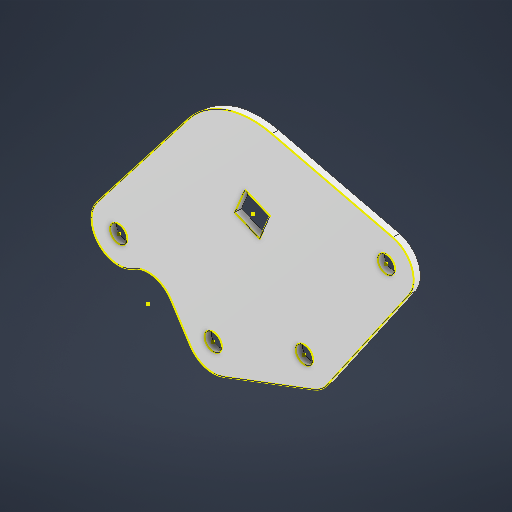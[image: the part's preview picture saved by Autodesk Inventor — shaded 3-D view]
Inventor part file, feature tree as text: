
AUTODESK INVENTOR PART (.ipt)
format: ipt  version: 2025 (Build 290162010, 162A)  size: 266,240 bytes
history: native  units: in
note: dims shown in document units (in); Inventor stores cm internally (conversion verified against a paired STEP export)
features: reference x7, other x6, sketch x2, sheet_metal_op x1
ambient origin geometry x8: Origin, YZ Plane, XZ Plane, XY Plane, X Axis, Y Axis, Z Axis, Center Point
bodies: Solid1 (feature_tree)
feature tree (16):
  sheet_metal_op  "Face1"
  sketch  "Sketch2"  dims[d3=0.16in d5=1.25in d6=0.16in d7=0.0687in d8=0.16in d10=0.16in d11=0.5in d12=0.5in d13=0.5in d14=0.16in d16=1.5in d17=0.5in d18=0.3624in d19=0.5in d20=0.0625in]
  sketch  "Sketch1"  dims[d0=2.5in]
  reference  "Reference1"
  reference  "Reference2"
  reference  "Reference3"
  reference  "Reference4"
  reference  "Reference5"
  reference  "Reference6"
  reference  "Reference7"
  other  "Plate1"
  parser-record x1  (decoder bookkeeping rows leaked as tree rows — omitted from the tree; the rows remain in map.json)
  other  "ACE 2.0.iam"
  other  "Shaft Collar without Set Screw:27"
  other  "V5 Rotation Sensor:1"
  other  "Insert Circle:16"
note: 1 file-system path scrubbed to <path> (originals preserved in map.json)
